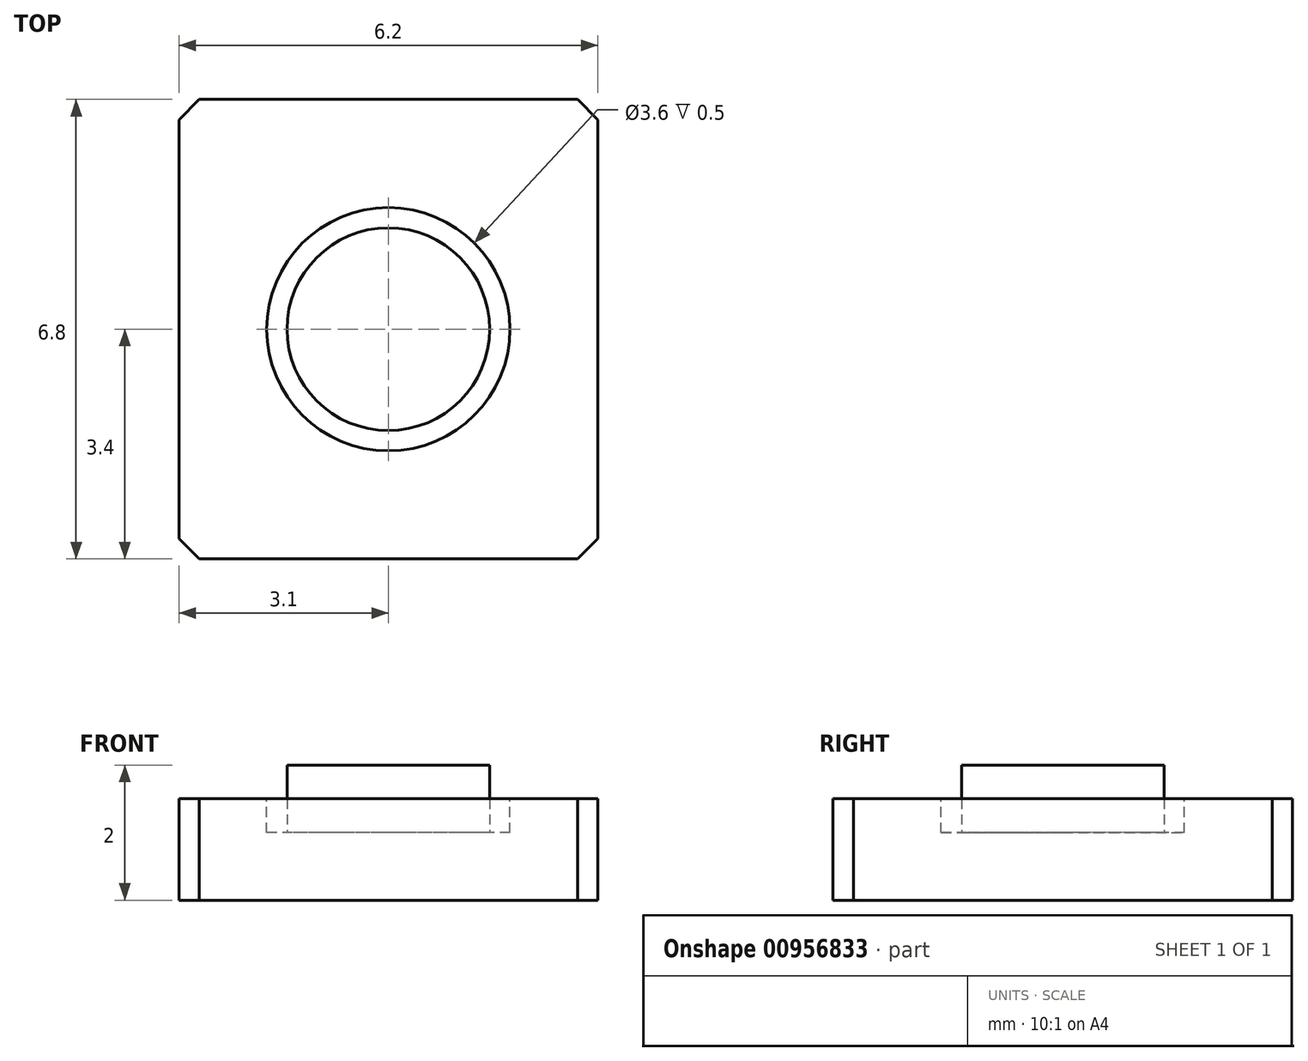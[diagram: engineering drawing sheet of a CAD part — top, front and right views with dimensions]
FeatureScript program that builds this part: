
annotation { "Feature Type Name" : "Feature", "Feature Type Description" : "" }
export const myFeature = defineFeature(function(context is Context, id is Id, definition is map)
    precondition{}
    {
        {
            var Q0;
            Q0=qCreatedBy(makeId("Top.planeOp"),FACE);
            var sketch = newSketch(context, id + "F0", { "sketchPlane" : qUnion([Q0])});
            skLineSegment(sketch, "E0.bottom", {"start": v(3.1, 3.4) * mm, "end": v(-3.1, 3.4) * mm});
            skLineSegment(sketch, "E0.top", {"start": v(3.1, -3.4) * mm, "end": v(-3.1, -3.4) * mm});
            skLineSegment(sketch, "E0.left", {"start": v(3.1, 3.4) * mm, "end": v(3.1, -3.4) * mm});
            skLineSegment(sketch, "E0.right", {"start": v(-3.1, 3.4) * mm, "end": v(-3.1, -3.4) * mm});
            skPoint(sketch, "E0.middle", {"position": v(0, 0) * mm});
            skSolve(sketch);
        }
        {
            var Q0;
            Q0=qSketchRegion(id+"F0",true);
            extrude(context, id + "F1", {"entities" : qUnion([Q0]), "depth" : 1.5 * mm, "offsetDistance" : 25 * mm});
        }
        {
            var Q0;
            Q0=makeQuery(id+"F1.opExtrude","CAP_FACE",FACE,{"disambiguationData":[OSD([sQuery(id+"F0.wireOp",EDGE,"E0.bottom"),sQuery(id+"F0.wireOp",EDGE,"E0.top"),sQuery(id+"F0.wireOp",EDGE,"E0.left"),sQuery(id+"F0.wireOp",EDGE,"E0.right")])],"isStart":false});
            var sketch = newSketch(context, id + "F2", { "sketchPlane" : qUnion([Q0])});
            skCircle(sketch, "E1", {"center": v(0, 0) * mm, "radius": 1.8 * mm});
            skSolve(sketch);
        }
        {
            var Q0;
            Q0=qSketchRegion(id+"F2",true);
            extrude(context, id + "F3", {"entities" : qUnion([Q0]), "operationType" : NewBodyOperationType.REMOVE, "oppositeDirection" : true, "depth" : .5 * mm, "offsetDistance" : 25 * mm});
        }
        {
            var Q0;
            Q0=makeQuery(id+"F3.boolean.opBoolean","COPY",FACE,{"derivedFrom":makeQuery(id+"F3.opExtrude","CAP_FACE",FACE,{"disambiguationData":[OSD([sQuery(id+"F2.wireOp",EDGE,"E1")])],"isStart":false})});
            var sketch = newSketch(context, id + "F4", { "sketchPlane" : qUnion([Q0])});
            skCircle(sketch, "E2", {"center": v(0, 0) * mm, "radius": 1.5 * mm});
            skSolve(sketch);
        }
        {
            var Q0;
            Q0=qSketchRegion(id+"F4",true);
            extrude(context, id + "F5", {"entities" : qUnion([Q0]), "operationType" : NewBodyOperationType.ADD, "depth" : 1 * mm, "offsetDistance" : 25 * mm});
        }
        {
            var Q0;
            Q0=makeQuery(id+"F1.opExtrude","SWEPT_EDGE",EDGE,{"disambiguationData":[OSD([sQuery(id+"F0.wireOp",EDGE,"E0.top"),sQuery(id+"F0.wireOp",EDGE,"E0.right")])]});
            var Q1;
            Q1=makeQuery(id+"F1.opExtrude","SWEPT_EDGE",EDGE,{"disambiguationData":[OSD([sQuery(id+"F0.wireOp",EDGE,"E0.top"),sQuery(id+"F0.wireOp",EDGE,"E0.left")])]});
            var Q2;
            Q2=makeQuery(id+"F1.opExtrude","SWEPT_EDGE",EDGE,{"disambiguationData":[OSD([sQuery(id+"F0.wireOp",EDGE,"E0.bottom"),sQuery(id+"F0.wireOp",EDGE,"E0.left")])]});
            var Q3;
            Q3=makeQuery(id+"F1.opExtrude","SWEPT_EDGE",EDGE,{"disambiguationData":[OSD([sQuery(id+"F0.wireOp",EDGE,"E0.bottom"),sQuery(id+"F0.wireOp",EDGE,"E0.right")])]});
            chamfer(context, id + "F6", {"entities" : qUnion([Q0, Q1, Q2, Q3]), "width" : .3 * mm, "tangentPropagation" : true});
        }
    });
